# Revit family: MADEL_GRILL_AIR RETURN_FIXED BLADES 45º_DMT+(PLRX - PLRXL) – (1.D1)
name_source: partatom
category: Terminales de aire
revit_build: Autodesk Revit 2015 (Build: 20140606_1530(x64)
units: mm (PartAtom-declared; Revit-internal decimal feet)

## types (1)
- MADEL_GRILL_AIR RETURN_FIXED BLADES 45º_DMT+(PLRX - PLRXL) – (1.D1)
    Afree = 0.0885 m²
    B = 530 mm
    BIMETRICAL = http://www.bimetrical.com
    BIMETRICAL Category = AirTerminal
    Blade Lenght = 485 mm  [stored 1.59121 ft]
    Comentarios de tipo = The DMT series grilles are designed to be used in extractors of cold and hot air. They are mounted on walls or in false ceilings.
    D1 = 248 mm
    D_Connector = 250 mm  [stored 0.82021 ft]
    Descripción = MADEL_Fixed blades air return grilles
    E = 320 mm  [stored 1.04987 ft]
    Fabricante = MADEL
    Family Version = 1.0
    Flujo máx. = 956 m³/h
    Flujo mín. = 478 m³/h
    H = 300 mm
    H1 = 285 mm  [stored 0.935039 ft]
    H2 = 31.7 mm
    IfcExportAs = IfcAirTerminalType
    IfcExportType = IfcAirTerminalType
    Imagen de tipo = <Ninguno>
    Kf = 0.126781
    L = 500 mm  [stored 1.64042 ft]
    L3 = 485 mm  [stored 1.59121 ft]
    Material Grill = MADEL_M9016
    Material Plenum Box = <Por categoría>
    Modelo = DMT-AR+PLRX 500x300
    N_Graphic lines = 8
    Nº  Blades = 11
    Nº Plenum Connections = 1
    PLRX = Sí
    PLRX/L = No
    Plenum Connection Type = Upper
    Product Size = 500x300
    Review Date = 11/2016
    Revit Version = Revit 2015 - English
    URL = http://www.madel.com
    Vmax = 3.0 m/s
    Vmed = 2.3 m/s
    Vmin = 1.5 m/s
    b_factor = -0.128138
    c_factor = -12.9322
    m_factor = 1.899495
    n_factor = 32.0898

note: [stored X ft] marks values corroborated as IEEE doubles in the binary element streams (Revit-internal decimal feet)

## geometry (parser evidence)
native form markers: Blend x4
no freeform markers — native parametric forms only
